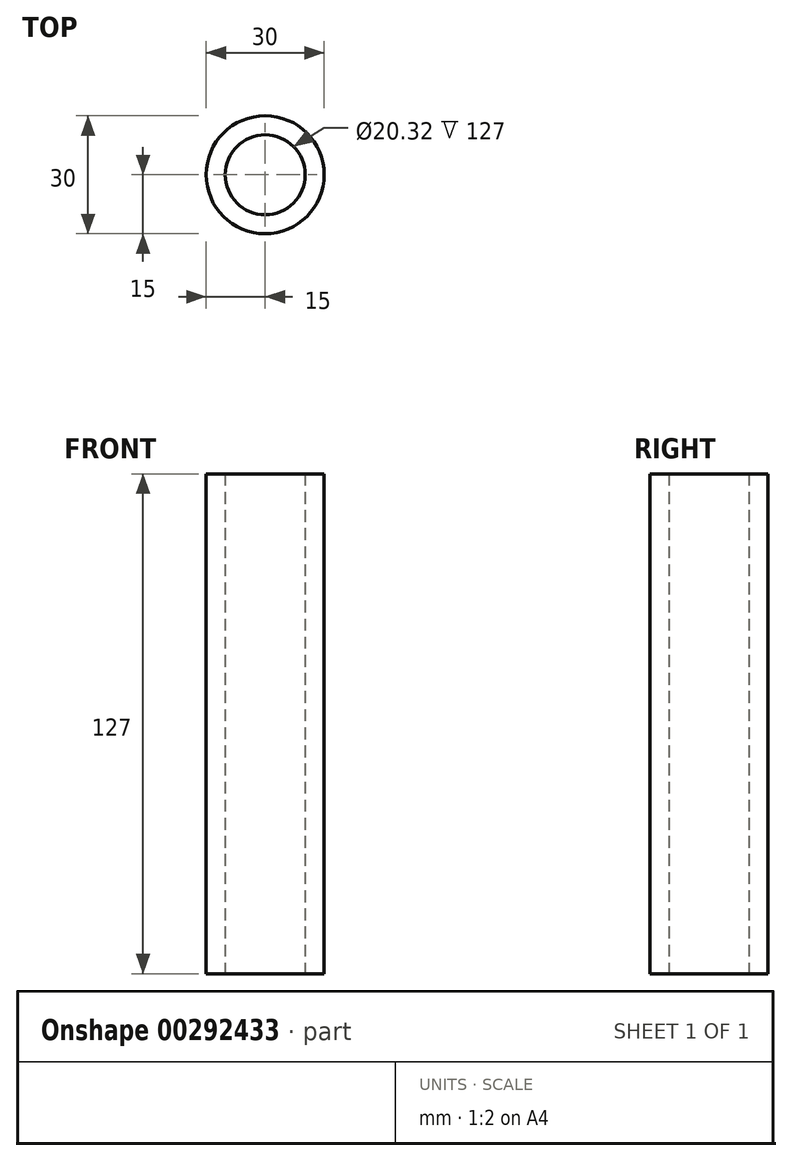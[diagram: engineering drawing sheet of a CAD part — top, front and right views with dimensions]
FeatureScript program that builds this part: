
annotation { "Feature Type Name" : "Feature", "Feature Type Description" : "" }
export const myFeature = defineFeature(function(context is Context, id is Id, definition is map)
    precondition{}
    {
        {
            var Q0;
            Q0=qCreatedBy(makeId("Top.planeOp"),FACE);
            var sketch = newSketch(context, id + "F0", { "sketchPlane" : qUnion([Q0])});
            skCircle(sketch, "E0", {"center": v(0, 0) * mm, "radius": 10.16 * mm});
            skCircle(sketch, "E1", {"center": v(0, 0) * mm, "radius": 15 * mm});
            skSolve(sketch);
        }
        {
            var Q0;
            Q0=makeQuery(id+"F0.imprint","IMPRINT",FACE,{"disambiguationData":[TD([[makeQuery(id+"F0.imprint","IMPRINT",EDGE,{"derivedFrom":sQuery(id+"F0.wireOp",EDGE,"E0")}),-1.0]])]});
            extrude(context, id + "F1", {"entities" : qUnion([Q0]), "depth" : 127 * mm});
        }
    });
